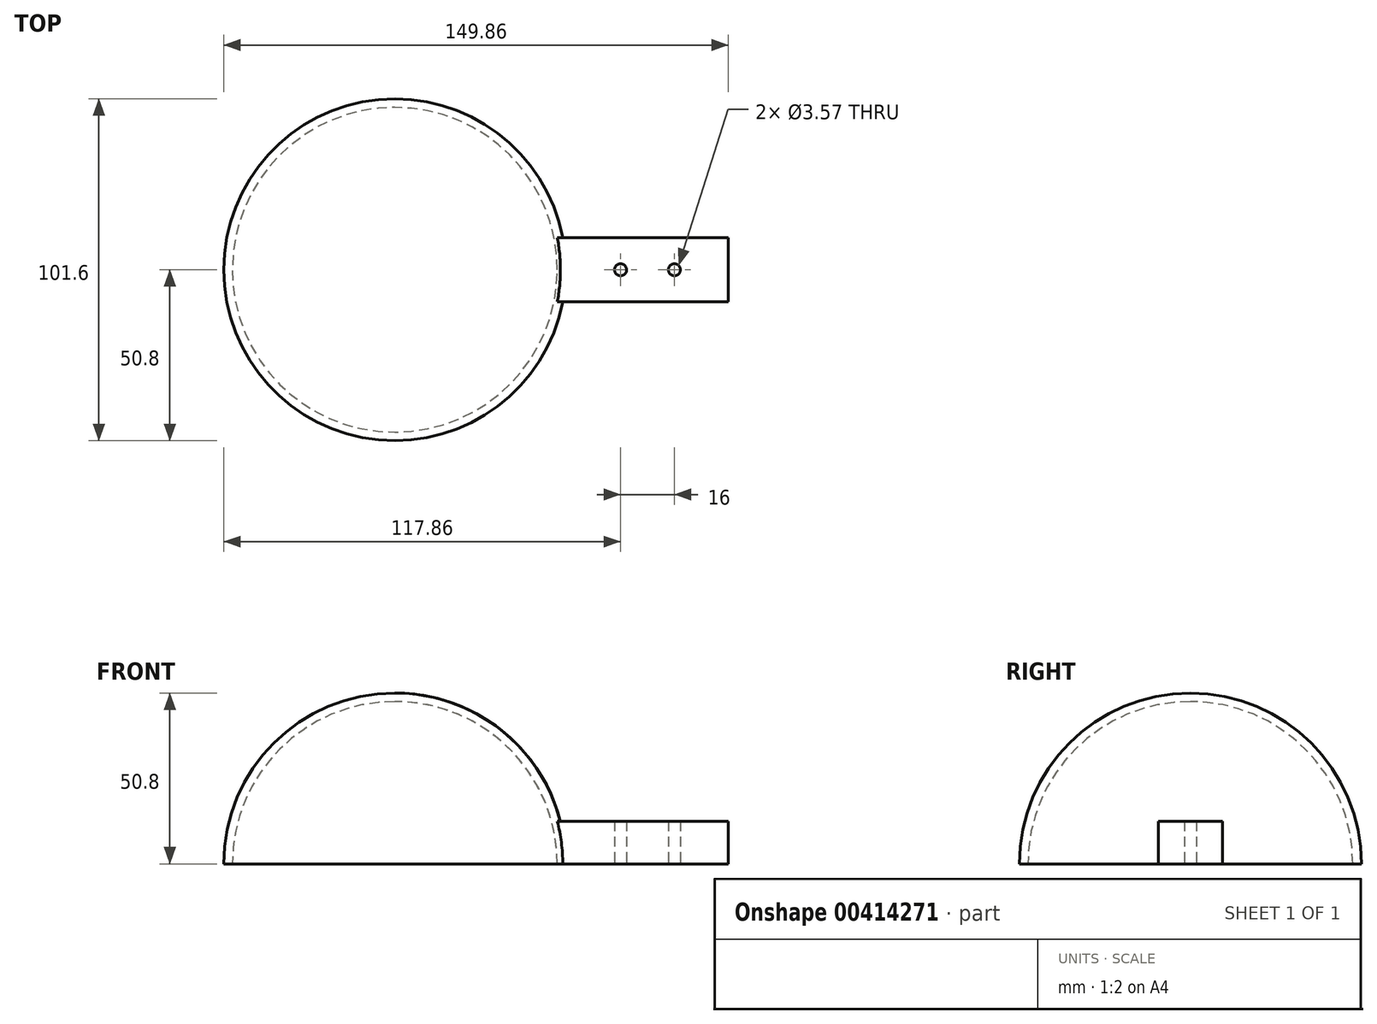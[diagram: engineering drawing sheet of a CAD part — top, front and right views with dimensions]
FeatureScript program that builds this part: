
annotation { "Feature Type Name" : "Feature", "Feature Type Description" : "" }
export const myFeature = defineFeature(function(context is Context, id is Id, definition is map)
    precondition{}
    {
        {
            var Q0;
            Q0=qCreatedBy(makeId("Top.planeOp"),FACE);
            var sketch = newSketch(context, id + "F0", { "sketchPlane" : qUnion([Q0])});
            skCircle(sketch, "E0", {"center": v(0, 0) * mm, "radius": 50.8 * mm});
            skSolve(sketch);
        }
        {
            var Q0;
            Q0=makeQuery(id+"F0.imprint","IMPRINT",FACE,{"disambiguationData":[TD([[makeQuery(id+"F0.imprint","IMPRINT",EDGE,{"derivedFrom":sQuery(id+"F0.wireOp",EDGE,"E0")}),1.0]])]});
            extrude(context, id + "F1", {"entities" : qUnion([Q0]), "depth" : 50.8 * mm});
        }
        {
            var Q0;
            Q0=makeQuery(id+"F1.opExtrude","CAP_FACE",FACE,{"disambiguationData":[OSD([sQuery(id+"F0.wireOp",EDGE,"E0")])],"isStart":false});
            fillet(context, id + "F2", {"entities" : qUnion([Q0]), "radius" : 50.8 * mm, "tangentPropagation" : true, "allowEdgeOverflow" : false});
        }
        {
            var Q0;
            Q0=makeQuery(id+"F1.opExtrude","CAP_FACE",FACE,{"disambiguationData":[OSD([sQuery(id+"F0.wireOp",EDGE,"E0")])],"isStart":true});
            shell(context, id + "F3", {"entities" : qUnion([Q0]), "thickness" : 2.54 * mm});
        }
        {
            var Q0;
            Q0=qCreatedBy(makeId("Top.planeOp"),FACE);
            var sketch = newSketch(context, id + "F4", { "sketchPlane" : qUnion([Q0])});
            skLineSegment(sketch, "E1.bottom", {"start": v(48.26, -9.52) * mm, "end": v(99.06, -9.52) * mm});
            skLineSegment(sketch, "E1.top", {"start": v(48.26, 9.53) * mm, "end": v(99.06, 9.53) * mm});
            skLineSegment(sketch, "E1.left", {"start": v(48.26, -9.52) * mm, "end": v(48.26, 9.53) * mm});
            skLineSegment(sketch, "E1.right", {"start": v(99.06, -9.52) * mm, "end": v(99.06, 9.53) * mm});
            skPoint(sketch, "E1.middle", {"position": v(73.66, 0) * mm});
            skSolve(sketch);
        }
        {
            var Q0;
            Q0=makeQuery(id+"F4.imprint","IMPRINT",FACE,{"disambiguationData":[TD([[makeQuery(id+"F4.imprint","IMPRINT",EDGE,{"derivedFrom":sQuery(id+"F4.wireOp",EDGE,"E1.bottom")}),1.0]])]});
            var sketch = newSketch(context, id + "F5", { "sketchPlane" : qUnion([Q0])});
            skSolve(sketch);
        }
        {
            var Q0;
            Q0=makeQuery(id+"F4.imprint","IMPRINT",FACE,{"disambiguationData":[TD([[makeQuery(id+"F4.imprint","IMPRINT",EDGE,{"derivedFrom":sQuery(id+"F4.wireOp",EDGE,"E1.bottom")}),1.0]])]});
            extrude(context, id + "F6", {"entities" : qUnion([Q0]), "operationType" : NewBodyOperationType.ADD, "depth" : 12.7 * mm});
        }
        {
            var Q0;
            Q0=makeQuery(id+"F5.imprint","IMPRINT",FACE,{"disambiguationData":[TD([[makeQuery(id+"F5.imprint","IMPRINT",EDGE,{"derivedFrom":makeQuery(id+"F4.imprint","IMPRINT",EDGE,{"derivedFrom":sQuery(id+"F4.wireOp",EDGE,"E1.bottom")})}),1.0]])]});
            var sketch = newSketch(context, id + "F7", { "sketchPlane" : qUnion([Q0])});
            skPoint(sketch, "E2", {"position": v(67.06, 0) * mm});
            skPoint(sketch, "E3", {"position": v(83.06, 0) * mm});
            skSolve(sketch);
        }
        {
            var Q0;
            Q0=sQuery(id+"F7.wireOp",VERTEX,"E3");
            var Q1;
            Q1=sQuery(id+"F7.wireOp",VERTEX,"E2");
            var Q2;
            Q2=makeQuery(id+"F1.opExtrude","SWEPT_BODY",BODY,{"disambiguationData":[OSD([sQuery(id+"F0.wireOp",EDGE,"E0")])]});
            hole(context, id + "F8", {"style" : HoleStyle.SIMPLE, "endStyle" : HoleEndStyle.THROUGH, "oppositeDirection" : true, "holeDiameter" : 3.57 * mm, "isTappedThrough" : true, "tappedDepth" : 12.7 * mm, "tapClearance" : 3, "locations" : qUnion([Q0, Q1]), "scope" : qUnion([Q2])});
        }
    });
